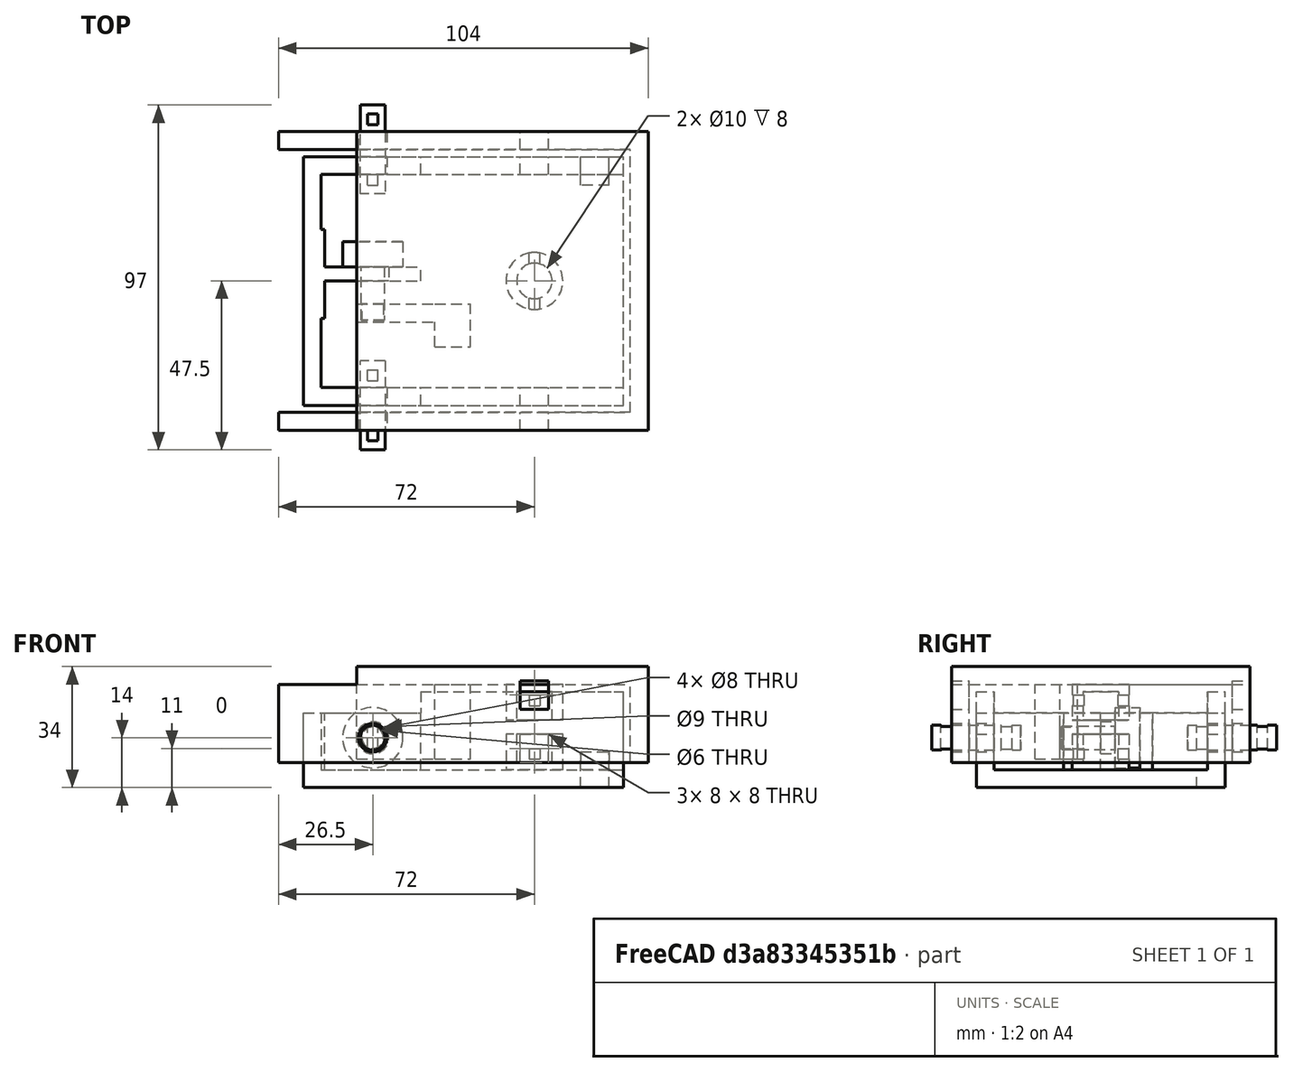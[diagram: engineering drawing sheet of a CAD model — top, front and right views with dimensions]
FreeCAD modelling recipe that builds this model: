
FCSTD DOCUMENT  (FreeCAD 0.20R29410 (Git))
Label: GuitarPedal
License: All rights reserved
LicenseURL: http://en.wikipedia.org/wiki/All_rights_reserved
objects: Part::Box×21, Part::Cylinder×12, Part::MultiFuse×11, Part::Cut×9, Spreadsheet::Sheet×1, Part::Compound×1
note: 54 computed .brp shape members not serialized (recipe doc carries the construction recipe); baked Part::Feature solids carry a one-line shape summary decoded from their .brp

FEATURE [Spreadsheet::Sheet] Spreadsheet  label="SS"
  cells = A2=PedalWidth; B2(PedalWidth)==70mm; A3=PedalHeight; B3(PedalHeight)==27mm; A4=PedalLength; B4(PedalLength)==90mm; A5=PedalBodyThickness; B5(PedalBodyThickness)==5mm; A6=TopClearance; B6(TopClearance)==2mm; A7=PedalTopHeight; B7(PedalTopHeight)==25mm; A8=PedalHingeBite; B8(PedalHingeBite)==6mm; A10=PivotRodHoleDiameter; B10(PivotRodHoleDiameter)==8mm; A11=PivotRodHoleClearance; B11(PivotRodHoleClearance)==0.5mm; A12=PivotRodLength; B12(PivotRodLength)==25mm; A13=PivotRodPinholeDiameter; B13(PivotRodPinholeDiameter)==3mm; A14=PivotRodPinholeOffset; B14(PivotRodPinholeOffset)==4mm; A16=PotentiometerHoleDiameter; B16(PotentiometerHoleDiameter)==9mm; A17=PotentiometerPlateThickness; B17(PotentiometerPlateThickness)==4mm; A18=PotentiometerPlateHeight; B18(PotentiometerPlateHeight)==18mm; A19=PotentiometerPlateLength; B19(PotentiometerPlateLength)==27mm; A20=PotentiometerPlateXPosition; B20(PotentiometerPlateXPosition)==6mm; A21=PotentiometerPlateBraceWidth; B21(PotentiometerPlateBraceWidth)==25mm; A22=PotentiometerPlateOffset; B22(PotentiometerPlateOffset)==2mm; A24=PivotHoleDiameter; B24(PivotHoleDiameter)==6mm; A25=PivotPlateThickness; B25(PivotPlateThickness)==5mm; A26=PivotPlateHeight; B26(PivotPlateHeight)==21mm; A27=PivotPlateLength; B27(PivotPlateLength)==22mm; A28=PivotPlateXPosition; B28(PivotPlateXPosition)==15mm; A29=PivotPlateBraceWidth; B29(PivotPlateBraceWidth)==12mm; A30=PivotPlateOffset; B30(PivotPlateOffset)==9mm; A32=WireHoleDiameter; B32(WireHoleDiameter)==4mm; A33=WireHoleLength; B33(WireHoleLength)==8mm; A34=PinInsertionHoleDiameter; B34(PinInsertionHoleDiameter)==8mm; A36=SpringHoleDiameter; B36(SpringHoleDiameter)==10mm; A37=SpringHoleXPosition; B37(SpringHoleXPosition)==65mm; A38=SpringHoleThickness; B38(SpringHoleThickness)==3mm; A39=SpringHoleHeight; B39(SpringHoleHeight)==8mm; A40=SplitHoleDiameter; B40(SplitHoleDiameter)==3mm; A41=SplitHoleSeatOffset; B41(SplitHoleSeatOffset)==1mm; A43=BottomSpringHoleRise; B43(BottomSpringHoleRise)==2mm; A44=TopSpringHoleDip; B44(TopSpringHoleDip)==2mm; A46=PotentiometerBodyDiameter; B46(PotentiometerBodyDiameter)==17mm; A47=PotentiometerBodyLength; B47(PotentiometerBodyLength)==7mm; A48=PotentiometerShaftDIameter; B48(PotentiometerShaftDiameter)==6.5mm; A49=PotentiometerShaftLength; B49(PotentiometerShaftLength)==15mm
FEATURE [Part::Box] Box  label="BottomPedalOutsideBody"
  AttacherType = Attacher::AttachEngine3D
  Height = 27
  Length = 90
  Width = 70
  expr: Height = <<SS>>.PedalHeight
  expr: Length = <<SS>>.PedalLength
  expr: Width = <<SS>>.PedalWidth
FEATURE [Part::Box] Box001  label="BottomPedalInsideBody"
  AttacherType = Attacher::AttachEngine3D
  Height = 22
  Length = 85
  Placement = pos=(5,5,5) rot=(0,0,1;0rad)
  Width = 60
  expr: .Placement.Base.x = <<SS>>.PedalBodyThickness
  expr: .Placement.Base.y = <<SS>>.PedalBodyThickness
  expr: .Placement.Base.z = <<SS>>.PedalBodyThickness
  expr: Height = <<SS>>.PedalHeight - <<SS>>.PedalBodyThickness
  expr: Length = <<SS>>.PedalLength - <<SS>>.PedalBodyThickness
  expr: Width = <<SS>>.PedalWidth - 2 * <<SS>>.PedalBodyThickness
FEATURE [Part::Box] Box002  label="TopPedalOutsideBody"
  AttacherType = Attacher::AttachEngine3D
  Height = 27
  Length = 104
  Placement = pos=(-7,-7,7) rot=(0,0,1;0rad)
  Width = 84
  expr: .Placement.Base.x = -<<SS>>.TopClearance - <<SS>>.PedalBodyThickness
  expr: .Placement.Base.y = -<<SS>>.TopClearance - <<SS>>.PedalBodyThickness
  expr: .Placement.Base.z = <<SS>>.PedalBodyThickness + <<SS>>.PedalHeight - <<SS>>.PedalTopHeight
  expr: Height = <<SS>>.PedalTopHeight + <<SS>>.TopClearance
  expr: Length = <<SS>>.PedalLength + 2 * (<<SS>>.TopClearance + <<SS>>.PedalBodyThickness)
  expr: Width = <<SS>>.PedalWidth + 2 * (<<SS>>.PedalBodyThickness + <<SS>>.TopClearance)
FEATURE [Part::Box] Box003  label="TopPedalInsideBody"
  AttacherType = Attacher::AttachEngine3D
  Height = 29
  Length = 99
  Placement = pos=(-7,-2,0) rot=(0,0,1;0rad)
  Width = 74
  expr: .Placement.Base.x = -<<SS>>.TopClearance - <<SS>>.PedalBodyThickness
  expr: .Placement.Base.y = -<<SS>>.TopClearance
  expr: Height = <<SS>>.PedalHeight + <<SS>>.TopClearance
  expr: Length = <<SS>>.PedalLength + 2 * <<SS>>.TopClearance + <<SS>>.PedalBodyThickness
  expr: Width = <<SS>>.PedalWidth + 2 * <<SS>>.TopClearance
FEATURE [Part::Cylinder] Cylinder  label="PivotAxisBottom"
  Angle = 360
  AttacherType = Attacher::AttachEngine3D
  FirstAngle = 0
  Height = 84
  Placement = pos=(19.5,77,14) rot=(1,0,0;1.5708rad)
  Radius = 4
  SecondAngle = 0
  expr: .Placement.Base.x = Spreadsheet.PotentiometerPlateXPosition + <<SS>>.PotentiometerPlateLength / 2
  expr: .Placement.Base.y = <<SS>>.PedalWidth + <<SS>>.PedalBodyThickness + <<SS>>.TopClearance
  expr: .Placement.Base.z = <<SS>>.PedalBodyThickness + <<SS>>.PotentiometerPlateHeight / 2
  expr: Height = <<SS>>.PedalWidth + 2 * <<SS>>.PedalBodyThickness + 2 * <<SS>>.TopClearance
  expr: Radius = <<SS>>.PivotRodHoleDiameter / 2
FEATURE [Part::Cylinder] Cylinder001  label="PivotAxisTop"
  Angle = 360
  AttacherType = Attacher::AttachEngine3D
  FirstAngle = 0
  Height = 84
  Placement = pos=(19.5,77,14) rot=(1,0,0;1.5708rad)
  Radius = 4
  SecondAngle = 0
  expr: .Placement.Base.x = Spreadsheet.PotentiometerPlateXPosition + <<SS>>.PotentiometerPlateLength / 2
  expr: .Placement.Base.y = <<SS>>.PedalWidth + <<SS>>.PedalBodyThickness + <<SS>>.TopClearance
  expr: .Placement.Base.z = <<SS>>.PedalBodyThickness + <<SS>>.PotentiometerPlateHeight / 2
  expr: Height = <<SS>>.PedalWidth + 2 * <<SS>>.PedalBodyThickness + 2 * <<SS>>.TopClearance
  expr: Radius = <<SS>>.PivotRodHoleDiameter / 2
FEATURE [Part::Box] Box004  label="PotentiometerPlate"
  AttacherType = Attacher::AttachEngine3D
  Height = 18
  Length = 27
  Placement = pos=(6,35,5) rot=(0,0,1;0rad)
  Width = 4
  expr: .Placement.Base.x = Spreadsheet.PotentiometerPlateXPosition
  expr: .Placement.Base.y = <<SS>>.PedalWidth / 2 - <<SS>>.PotentiometerPlateThickness / 2 + <<SS>>.PotentiometerPlateOffset
  expr: .Placement.Base.z = <<SS>>.PedalBodyThickness
  expr: Height = <<SS>>.PotentiometerPlateHeight
  expr: Length = <<SS>>.PotentiometerPlateLength
  expr: Width = <<SS>>.PotentiometerPlateThickness
FEATURE [Part::Box] Box005  label="PotentiometerPlateBrace"
  AttacherType = Attacher::AttachEngine3D
  Height = 18
  Length = 4
  Placement = pos=(2,24.5,5) rot=(0,0,1;0rad)
  Width = 25
  expr: .Placement.Base.x = Spreadsheet.PotentiometerPlateXPosition - <<SS>>.PotentiometerPlateThickness
  expr: .Placement.Base.y = <<SS>>.PedalWidth / 2 - <<SS>>.PotentiometerPlateBraceWidth / 2 + <<SS>>.PotentiometerPlateOffset
  expr: .Placement.Base.z = <<SS>>.PedalBodyThickness
  expr: Height = <<SS>>.PotentiometerPlateHeight
  expr: Length = <<SS>>.PotentiometerPlateThickness
  expr: Width = <<SS>>.PotentiometerPlateBraceWidth
FEATURE [Part::Cylinder] Cylinder002  label="PotentiometerMountingHole"
  Angle = 360
  AttacherType = Attacher::AttachEngine3D
  FirstAngle = 0
  Height = 4
  Placement = pos=(19.5,39,14) rot=(1,0,0;1.5708rad)
  Radius = 4.5
  SecondAngle = 0
  expr: .Placement.Base.x = Spreadsheet.PotentiometerPlateXPosition + <<SS>>.PotentiometerPlateLength / 2
  expr: .Placement.Base.y = <<SS>>.PedalWidth / 2 + <<SS>>.PotentiometerPlateThickness / 2 + <<SS>>.PotentiometerPlateOffset
  expr: .Placement.Base.z = <<SS>>.PedalBodyThickness + <<SS>>.PotentiometerPlateHeight / 2
  expr: Height = <<SS>>.PotentiometerPlateThickness
  expr: Radius = <<SS>>.PotentiometerHoleDiameter / 2
FEATURE [Part::MultiFuse] Fusion002  label="PotentiometerBracedBody"
  Shapes = -> [Box005,Box004]
FEATURE [Part::Cut] Cut002  label="PotentiometerMount"
  Base = -> Fusion002
  Tool = -> Cylinder002
FEATURE [Part::Box] Box006  label="PivotPlate"
  AttacherType = Attacher::AttachEngine3D
  Height = 21
  Length = 22
  Placement = pos=(15,23.5,8) rot=(0,0,1;0rad)
  Width = 5
  expr: .Placement.Base.x = Spreadsheet.PivotPlateXPosition
  expr: .Placement.Base.y = <<SS>>.PedalWidth / 2 - <<SS>>.PivotPlateThickness / 2 - <<SS>>.PivotPlateOffset
  expr: .Placement.Base.z = <<SS>>.PedalHeight + <<SS>>.TopClearance - <<SS>>.PivotPlateHeight
  expr: Height = <<SS>>.PivotPlateHeight
  expr: Length = <<SS>>.PivotPlateLength
  expr: Width = <<SS>>.PivotPlateThickness
FEATURE [Part::Box] Box007  label="PivotPlateBrace"
  AttacherType = Attacher::AttachEngine3D
  Height = 21
  Length = 10
  Placement = pos=(37,16.5,8) rot=(0,0,1;0rad)
  Width = 12
  expr: .Placement.Base.x = Spreadsheet.PivotPlateXPosition + <<SS>>.PivotPlateLength
  expr: .Placement.Base.y = <<SS>>.PedalWidth / 2 - <<SS>>.PivotPlateBraceWidth - <<SS>>.PivotPlateOffset + <<SS>>.PivotPlateThickness / 2
  expr: .Placement.Base.z = <<SS>>.PedalHeight + <<SS>>.TopClearance - <<SS>>.PivotPlateHeight
  expr: Height = <<SS>>.PivotPlateHeight
  expr: Length = <<SS>>.PivotPlateThickness * 2
  expr: Width = <<SS>>.PivotPlateBraceWidth
FEATURE [Part::Cylinder] Cylinder003  label="PivotMountingHole"
  Angle = 360
  AttacherType = Attacher::AttachEngine3D
  FirstAngle = 0
  Height = 5
  Placement = pos=(19.5,28.5,14) rot=(1,0,0;1.5708rad)
  Radius = 3
  SecondAngle = 0
  expr: .Placement.Base.x = Spreadsheet.PotentiometerPlateXPosition + <<SS>>.PotentiometerPlateLength / 2
  expr: .Placement.Base.y = <<SS>>.PedalWidth / 2 + <<SS>>.PivotPlateThickness / 2 - <<SS>>.PivotPlateOffset
  expr: .Placement.Base.z = <<SS>>.PedalBodyThickness + <<SS>>.PotentiometerPlateHeight / 2
  expr: Height = <<SS>>.PivotPlateThickness
  expr: Radius = <<SS>>.PivotHoleDiameter / 2
FEATURE [Part::MultiFuse] Fusion003  label="PivotBracedBody"
  Shapes = -> [Box007,Box006]
FEATURE [Part::Cut] Cut003  label="PivotMount"
  Base = -> Fusion003
  Tool = -> Cylinder003
FEATURE [Part::Box] Box008  label="WireHoleCutOut"
  AttacherType = Attacher::AttachEngine3D
  Height = 10
  Length = 8
  Placement = pos=(78,62,0) rot=(0,0,1;0rad)
  Width = 8
  expr: .Placement.Base.x = <<SS>>.PedalLength - 1.5 * <<SS>>.WireHoleLength
  expr: .Placement.Base.y = <<SS>>.PedalWidth - 2 * <<SS>>.WireHoleDiameter
  expr: .Placement.Base.z = 0mm
  expr: Height = 2 * <<SS>>.PedalBodyThickness
  expr: Length = <<SS>>.WireHoleLength
  expr: Width = <<SS>>.WireHoleDiameter * 2
FEATURE [Part::Cylinder] Cylinder004  label="BottomSpringHoleOuter"
  Angle = 360
  AttacherType = Attacher::AttachEngine3D
  FirstAngle = 0
  Height = 10
  Placement = pos=(65,35,5) rot=(0,0,1;0rad)
  Radius = 8
  SecondAngle = 0
  expr: .Placement.Base.x = <<SS>>.SpringHoleXPosition
  expr: .Placement.Base.y = <<SS>>.PedalWidth / 2
  expr: .Placement.Base.z = <<SS>>.PedalBodyThickness
  expr: Height = <<SS>>.SpringHoleHeight + <<SS>>.BottomSpringHoleRise
  expr: Radius = <<SS>>.SpringHoleDiameter / 2 + <<SS>>.SpringHoleThickness
FEATURE [Part::Cylinder] Cylinder005  label="BottomSpringHoleInner"
  Angle = 360
  AttacherType = Attacher::AttachEngine3D
  FirstAngle = 0
  Height = 8
  Placement = pos=(65,35,7) rot=(0,0,1;0rad)
  Radius = 5
  SecondAngle = 0
  expr: .Placement.Base.x = <<SS>>.SpringHoleXPosition
  expr: .Placement.Base.y = <<SS>>.PedalWidth / 2
  expr: .Placement.Base.z = <<SS>>.PedalBodyThickness + <<SS>>.BottomSpringHoleRise
  expr: Height = <<SS>>.SpringHoleHeight
  expr: Radius = <<SS>>.SpringHoleDiameter / 2
FEATURE [Part::Box] Box009  label="BottomSpringSplitPinHole"
  AttacherType = Attacher::AttachEngine3D
  Height = 3
  Length = 3
  Placement = pos=(63.5,27,8) rot=(0,0,1;0rad)
  Width = 16
  expr: .Placement.Base.x = <<SS>>.SpringHoleXPosition - <<SS>>.SplitHoleDiameter / 2
  expr: .Placement.Base.y = <<SS>>.PedalWidth / 2 - (<<SS>>.SpringHoleDiameter + 2 * <<SS>>.SpringHoleThickness) / 2
  expr: .Placement.Base.z = <<SS>>.PedalBodyThickness + <<SS>>.BottomSpringHoleRise + <<SS>>.SplitHoleSeatOffset
  expr: Height = <<SS>>.SplitHoleDiameter
  expr: Length = <<SS>>.SplitHoleDiameter
  expr: Width = <<SS>>.SpringHoleDiameter + 2 * <<SS>>.SpringHoleThickness
FEATURE [Part::MultiFuse] Fusion004  label="BottomSpringHoleCutout"
  Shapes = -> [Box009,Cylinder005]
FEATURE [Part::Cut] Cut004  label="BottomSpringCaptive"
  Base = -> Cylinder004
  Tool = -> Fusion004
FEATURE [Part::Box] Box010  label="TopSpringSplitPinHole"
  AttacherType = Attacher::AttachEngine3D
  Height = 3
  Length = 3
  Placement = pos=(63.5,27,23) rot=(0,0,1;0rad)
  Width = 16
  expr: .Placement.Base.x = <<SS>>.SpringHoleXPosition - <<SS>>.SplitHoleDiameter / 2
  expr: .Placement.Base.y = <<SS>>.PedalWidth / 2 - (<<SS>>.SpringHoleDiameter + 2 * <<SS>>.SpringHoleThickness) / 2
  expr: .Placement.Base.z = <<SS>>.PedalHeight + <<SS>>.TopClearance - <<SS>>.SplitHoleDiameter - <<SS>>.TopSpringHoleDip - <<SS>>.SplitHoleSeatOffset
  expr: Height = <<SS>>.SplitHoleDiameter
  expr: Length = <<SS>>.SplitHoleDiameter
  expr: Width = <<SS>>.SpringHoleDiameter + 2 * <<SS>>.SpringHoleThickness
FEATURE [Part::Cylinder] Cylinder006  label="TopSpringHoleOuter"
  Angle = 360
  AttacherType = Attacher::AttachEngine3D
  FirstAngle = 0
  Height = 10
  Placement = pos=(65,35,19) rot=(0,0,1;0rad)
  Radius = 8
  SecondAngle = 0
  expr: .Placement.Base.x = <<SS>>.SpringHoleXPosition
  expr: .Placement.Base.y = <<SS>>.PedalWidth / 2
  expr: .Placement.Base.z = <<SS>>.PedalHeight + <<SS>>.TopClearance - <<SS>>.SpringHoleHeight - <<SS>>.TopSpringHoleDip
  expr: Height = <<SS>>.SpringHoleHeight + <<SS>>.TopSpringHoleDip
  expr: Radius = <<SS>>.SpringHoleDiameter / 2 + <<SS>>.SpringHoleThickness
FEATURE [Part::Cylinder] Cylinder007  label="TopSpringHoleInner"
  Angle = 360
  AttacherType = Attacher::AttachEngine3D
  FirstAngle = 0
  Height = 8
  Placement = pos=(65,35,19) rot=(0,0,1;0rad)
  Radius = 5
  SecondAngle = 0
  expr: .Placement.Base.x = <<SS>>.SpringHoleXPosition
  expr: .Placement.Base.y = <<SS>>.PedalWidth / 2
  expr: .Placement.Base.z = <<SS>>.PedalHeight + <<SS>>.TopClearance - <<SS>>.SpringHoleHeight - <<SS>>.TopSpringHoleDip
  expr: Height = <<SS>>.SpringHoleHeight
  expr: Radius = <<SS>>.SpringHoleDiameter / 2
FEATURE [Part::MultiFuse] Fusion005  label="TopSpringHoleCutout"
  Shapes = -> [Box010,Cylinder007]
FEATURE [Part::Cut] Cut005  label="TopSpringCaptive"
  Base = -> Cylinder006
  Tool = -> Fusion005
FEATURE [Part::Cylinder] Cylinder008  label="PivotRodBodyLeft"
  Angle = 360
  AttacherType = Attacher::AttachEngine3D
  FirstAngle = 0
  Height = 25
  Placement = pos=(19.5,12.5,14) rot=(1,0,0;1.5708rad)
  Radius = 3.5
  SecondAngle = 0
  expr: .Placement.Base.x = Spreadsheet.PotentiometerPlateXPosition + <<SS>>.PotentiometerPlateLength / 2
  expr: .Placement.Base.y = <<SS>>.PivotRodLength / 2
  expr: .Placement.Base.z = <<SS>>.PedalBodyThickness + <<SS>>.PotentiometerPlateHeight / 2
  expr: Height = <<SS>>.PivotRodLength
  expr: Radius = <<SS>>.PivotRodHoleDiameter / 2 - <<SS>>.PivotRodHoleClearance
FEATURE [Part::Box] Box011  label="PivotRodBodyPinhole1"
  AttacherType = Attacher::AttachEngine3D
  Height = 8
  Length = 3
  Placement = pos=(18,7,10) rot=(0,0,1;0rad)
  Width = 3
  expr: .Placement.Base.x = Spreadsheet.PotentiometerPlateXPosition + <<SS>>.PotentiometerPlateLength / 2 - <<SS>>.PivotRodPinholeDiameter / 2
  expr: .Placement.Base.y = <<SS>>.PivotRodLength / 2 - <<SS>>.PivotRodPinholeOffset - <<SS>>.PivotRodPinholeDiameter / 2
  expr: .Placement.Base.z = <<SS>>.PedalBodyThickness + <<SS>>.PotentiometerPlateHeight / 2 - <<SS>>.PivotRodHoleDiameter / 2
  expr: Height = <<SS>>.PivotRodHoleDiameter
  expr: Length = <<SS>>.PivotRodPinholeDiameter
  expr: Width = <<SS>>.PivotRodPinholeDiameter
FEATURE [Part::Box] Box012  label="PivotRodBodyPinhole2"
  AttacherType = Attacher::AttachEngine3D
  Height = 8
  Length = 3
  Placement = pos=(18,-10,10) rot=(0,0,1;0rad)
  Width = 3
  expr: .Placement.Base.x = Spreadsheet.PotentiometerPlateXPosition + <<SS>>.PotentiometerPlateLength / 2 - <<SS>>.PivotRodPinholeDiameter / 2
  expr: .Placement.Base.y = <<SS>>.PivotRodLength / 2 + <<SS>>.PivotRodPinholeOffset - <<SS>>.PivotRodPinholeDiameter / 2 - <<SS>>.PivotRodLength
  expr: .Placement.Base.z = <<SS>>.PedalBodyThickness + <<SS>>.PotentiometerPlateHeight / 2 - <<SS>>.PivotRodHoleDiameter / 2
  expr: Height = <<SS>>.PivotRodHoleDiameter
  expr: Length = <<SS>>.PivotRodPinholeDiameter
  expr: Width = <<SS>>.PivotRodPinholeDiameter
FEATURE [Part::MultiFuse] Fusion008  label="PivotRodPinholesLeft"
  Shapes = -> [Box011,Box012]
FEATURE [Part::Cut] Cut006  label="PivotRodLeft"
  Base = -> Cylinder008
  Tool = -> Fusion008
FEATURE [Part::Box] Box013  label="PivotRodBodyPinhole3"
  AttacherType = Attacher::AttachEngine3D
  Height = 8
  Length = 3
  Placement = pos=(18,79,10) rot=(0,0,1;0rad)
  Width = 3
  expr: .Placement.Base.x = Spreadsheet.PotentiometerPlateXPosition + <<SS>>.PotentiometerPlateLength / 2 - <<SS>>.PivotRodPinholeDiameter / 2
  expr: .Placement.Base.y = <<SS>>.PivotRodLength / 2 - <<SS>>.PivotRodPinholeOffset - <<SS>>.PivotRodPinholeDiameter / 2 + +<<SS>>.PedalWidth + <<SS>>.TopClearance
  expr: .Placement.Base.z = <<SS>>.PedalBodyThickness + <<SS>>.PotentiometerPlateHeight / 2 - <<SS>>.PivotRodHoleDiameter / 2
  expr: Height = <<SS>>.PivotRodHoleDiameter
  expr: Length = <<SS>>.PivotRodPinholeDiameter
  expr: Width = <<SS>>.PivotRodPinholeDiameter
FEATURE [Part::Box] Box014  label="PivotRodBodyPinhole4"
  AttacherType = Attacher::AttachEngine3D
  Height = 8
  Length = 3
  Placement = pos=(18,62,10) rot=(0,0,1;0rad)
  Width = 3
  expr: .Placement.Base.x = Spreadsheet.PotentiometerPlateXPosition + <<SS>>.PotentiometerPlateLength / 2 - <<SS>>.PivotRodPinholeDiameter / 2
  expr: .Placement.Base.y = <<SS>>.PivotRodLength / 2 + <<SS>>.PivotRodPinholeOffset - <<SS>>.PivotRodPinholeDiameter / 2 - <<SS>>.PivotRodLength + +<<SS>>.PedalWidth + <<SS>>.TopClearance
  expr: .Placement.Base.z = <<SS>>.PedalBodyThickness + <<SS>>.PotentiometerPlateHeight / 2 - <<SS>>.PivotRodHoleDiameter / 2
  expr: Height = <<SS>>.PivotRodHoleDiameter
  expr: Length = <<SS>>.PivotRodPinholeDiameter
  expr: Width = <<SS>>.PivotRodPinholeDiameter
FEATURE [Part::Cylinder] Cylinder009  label="PivotRodBodyRight"
  Angle = 360
  AttacherType = Attacher::AttachEngine3D
  FirstAngle = 0
  Height = 25
  Placement = pos=(19.5,84.5,14) rot=(1,0,0;1.5708rad)
  Radius = 3.5
  SecondAngle = 0
  expr: .Placement.Base.x = Spreadsheet.PotentiometerPlateXPosition + <<SS>>.PotentiometerPlateLength / 2
  expr: .Placement.Base.y = <<SS>>.PivotRodLength / 2 + <<SS>>.PedalWidth + <<SS>>.TopClearance
  expr: .Placement.Base.z = <<SS>>.PedalBodyThickness + <<SS>>.PotentiometerPlateHeight / 2
  expr: Height = <<SS>>.PivotRodLength
  expr: Radius = <<SS>>.PivotRodHoleDiameter / 2 - <<SS>>.PivotRodHoleClearance
FEATURE [Part::MultiFuse] Fusion009  label="PivotRodPinholesRight"
  Shapes = -> [Box013,Box014]
FEATURE [Part::Cut] Cut007  label="PivotRodRight"
  Base = -> Cylinder009
  Tool = -> Fusion009
FEATURE [Part::Box] Box015  label="BottomSpringSplitPinHole1"
  AttacherType = Attacher::AttachEngine3D
  Height = 8
  Length = 8
  Placement = pos=(61,65,7) rot=(0,0,1;0rad)
  Width = 5
  expr: .Placement.Base.x = <<SS>>.SpringHoleXPosition - <<SS>>.PinInsertionHoleDiameter / 2
  expr: .Placement.Base.y = <<SS>>.PedalWidth - <<SS>>.PedalBodyThickness
  expr: .Placement.Base.z = <<SS>>.PedalBodyThickness + <<SS>>.BottomSpringHoleRise
  expr: Height = <<SS>>.PinInsertionHoleDiameter
  expr: Length = <<SS>>.PinInsertionHoleDiameter
  expr: Width = <<SS>>.PedalBodyThickness
FEATURE [Part::Box] Box016  label="BottomSpringSplitPinHole2"
  AttacherType = Attacher::AttachEngine3D
  Height = 8
  Length = 8
  Placement = pos=(61,0,7) rot=(0,0,1;0rad)
  Width = 5
  expr: .Placement.Base.x = <<SS>>.SpringHoleXPosition - <<SS>>.PinInsertionHoleDiameter / 2
  expr: .Placement.Base.y = 0mm
  expr: .Placement.Base.z = <<SS>>.PedalBodyThickness + <<SS>>.BottomSpringHoleRise
  expr: Height = <<SS>>.PinInsertionHoleDiameter
  expr: Length = <<SS>>.PinInsertionHoleDiameter
  expr: Width = <<SS>>.PedalBodyThickness
FEATURE [Part::MultiFuse] Fusion  label="BottomPedalCutout"
  Shapes = -> [Cylinder,Box001,Box008,Box015,Box016]
FEATURE [Part::Cut] Cut  label="PedalBodyBottom"
  Base = -> Box
  Tool = -> Fusion
FEATURE [Part::MultiFuse] Fusion007  label="BottomPedalPreHingeCutout"
  Shapes = -> [Cut004,Cut002,Cut]
FEATURE [Part::Box] Box017  label="TopSpringSplitPinHole1"
  AttacherType = Attacher::AttachEngine3D
  Height = 8
  Length = 8
  Placement = pos=(61,72,22) rot=(0,0,1;0rad)
  Width = 5
  expr: .Placement.Base.x = <<SS>>.SpringHoleXPosition - <<SS>>.PinInsertionHoleDiameter / 2
  expr: .Placement.Base.y = <<SS>>.PedalWidth + <<SS>>.TopClearance
  expr: .Placement.Base.z = <<SS>>.PedalHeight + <<SS>>.TopClearance - <<SS>>.PinInsertionHoleDiameter / 2 - <<SS>>.TopSpringHoleDip - <<SS>>.SplitHoleSeatOffset
  expr: Height = <<SS>>.PinInsertionHoleDiameter
  expr: Length = <<SS>>.PinInsertionHoleDiameter
  expr: Width = <<SS>>.PedalBodyThickness
FEATURE [Part::Box] Box018  label="TopSpringSplitPinHole2"
  AttacherType = Attacher::AttachEngine3D
  Height = 8
  Length = 8
  Placement = pos=(61,-7,22) rot=(0,0,1;0rad)
  Width = 5
  expr: .Placement.Base.x = <<SS>>.SpringHoleXPosition - <<SS>>.PinInsertionHoleDiameter / 2
  expr: .Placement.Base.y = -<<SS>>.TopClearance - <<SS>>.PedalBodyThickness
  expr: .Placement.Base.z = <<SS>>.PedalHeight + <<SS>>.TopClearance - <<SS>>.PinInsertionHoleDiameter / 2 - <<SS>>.TopSpringHoleDip - <<SS>>.SplitHoleSeatOffset
  expr: Height = <<SS>>.PinInsertionHoleDiameter
  expr: Length = <<SS>>.PinInsertionHoleDiameter
  expr: Width = <<SS>>.PedalBodyThickness
FEATURE [Part::Cylinder] Cylinder010  label="PotentiometerBody"
  Angle = 360
  AttacherType = Attacher::AttachEngine3D
  FirstAngle = 0
  Height = 7
  Placement = pos=(19.5,46,14) rot=(1,0,0;1.5708rad)
  Radius = 8.5
  SecondAngle = 0
  expr: .Placement.Base.x = Spreadsheet.PotentiometerPlateXPosition + <<SS>>.PotentiometerPlateLength / 2
  expr: .Placement.Base.y = <<SS>>.PedalWidth / 2 + <<SS>>.PotentiometerPlateThickness / 2 + <<SS>>.PotentiometerPlateOffset + <<SS>>.PotentiometerBodyLength
  expr: .Placement.Base.z = <<SS>>.PedalBodyThickness + <<SS>>.PotentiometerPlateHeight / 2
  expr: Height = <<SS>>.PotentiometerBodyLength
  expr: Radius = <<SS>>.PotentiometerBodyDiameter / 2
FEATURE [Part::Cylinder] Cylinder011  label="PotentiometerShaft"
  Angle = 360
  AttacherType = Attacher::AttachEngine3D
  FirstAngle = 0
  Height = 15
  Placement = pos=(19.5,39,14) rot=(1,0,0;1.5708rad)
  Radius = 3.25
  SecondAngle = 0
  expr: .Placement.Base.x = Spreadsheet.PotentiometerPlateXPosition + <<SS>>.PotentiometerPlateLength / 2
  expr: .Placement.Base.y = <<SS>>.PedalWidth / 2 + <<SS>>.PotentiometerPlateThickness / 2 + <<SS>>.PotentiometerPlateOffset
  expr: .Placement.Base.z = <<SS>>.PedalBodyThickness + <<SS>>.PotentiometerPlateHeight / 2
  expr: Height = <<SS>>.PotentiometerShaftLength
  expr: Radius = <<SS>>.PotentiometerShaftDiameter / 2
FEATURE [Part::MultiFuse] Fusion010  label="Potentiometer"
  Shapes = -> [Cylinder011,Cylinder010]
FEATURE [Part::Box] Box019  label="TopPedalHingeCutout"
  AttacherType = Attacher::AttachEngine3D
  Height = 5
  Length = 22
  Placement = pos=(-7,-7,29) rot=(0,0,1;0rad)
  Width = 84
  expr: .Placement.Base.x = -<<SS>>.TopClearance - <<SS>>.PedalBodyThickness
  expr: .Placement.Base.y = -<<SS>>.TopClearance - <<SS>>.PedalBodyThickness
  expr: .Placement.Base.z = <<SS>>.PedalHeight + <<SS>>.TopClearance
  expr: Height = <<SS>>.PedalBodyThickness
  expr: Length = <<SS>>.PivotPlateXPosition + <<SS>>.PedalBodyThickness + <<SS>>.TopClearance
  expr: Width = <<SS>>.PedalWidth + 2 * (<<SS>>.PedalBodyThickness + <<SS>>.TopClearance)
FEATURE [Part::MultiFuse] Fusion001  label="TopPedalCutout"
  Shapes = -> [Box003,Cylinder001,Box017,Box018,Box019]
FEATURE [Part::Cut] Cut001  label="PedalBodyTop"
  Base = -> Box002
  Tool = -> Fusion001
FEATURE [Part::MultiFuse] Fusion006  label="TopPedalPreRotate"
  Placement = pos=(-19.5,0,-14) rot=(0,1,0;0rad)
  Shapes = -> [Cut001,Cut003,Cut005]
  expr: .Placement.Base.x = -Spreadsheet.PotentiometerPlateXPosition - <<SS>>.PotentiometerPlateLength / 2
  expr: .Placement.Base.z = -<<SS>>.PedalBodyThickness - <<SS>>.PotentiometerPlateHeight / 2
FEATURE [Part::Box] Box020  label="BottomPedalHingeCutout"
  AttacherType = Attacher::AttachEngine3D
  Height = 6
  Length = 33
  Placement = pos=(0,0,21) rot=(0,0,1;0rad)
  Width = 70
  expr: .Placement.Base.z = <<SS>>.PedalHeight - <<SS>>.PedalHingeBite
  expr: Height = <<SS>>.PedalHingeBite
  expr: Length = <<SS>>.PotentiometerPlateXPosition + <<SS>>.PotentiometerPlateLength
  expr: Width = <<SS>>.PedalWidth
FEATURE [Part::Compound] Compound  label="TopPedal"
  Links = -> [Fusion006]
  Placement = pos=(19.5,0,14) rot=(0,-1,0;0rad)
  expr: .Placement.Base.x = Spreadsheet.PotentiometerPlateXPosition + <<SS>>.PotentiometerPlateLength / 2
  expr: .Placement.Base.z = <<SS>>.PedalBodyThickness + <<SS>>.PotentiometerPlateHeight / 2
FEATURE [Part::Cut] Cut008  label="BottomPedal"
  Base = -> Fusion007
  Tool = -> Box020
